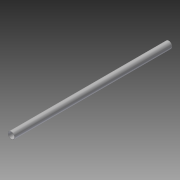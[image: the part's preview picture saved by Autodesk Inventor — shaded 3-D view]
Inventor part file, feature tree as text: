
AUTODESK INVENTOR PART (.ipt)
format: ipt  version: 2013 (Build 170138000, 138)  size: 70,144 bytes
history: native  units: in
note: dims shown in document units (in); Inventor stores cm internally (conversion verified against a paired STEP export)
features: extrude x1, sketch x1
ambient origin geometry x8: Origin, YZ Plane, XZ Plane, XY Plane, X Axis, Y Axis, Z Axis, Center Point
bodies: Solid1 (feature_tree)
feature tree (2):
  extrude  "Extrusion1"  Depth=1.37in
  sketch  "Sketch1"  dims[d0=1.5in d2=1.37in d3=34.63in d4=0.0in]
